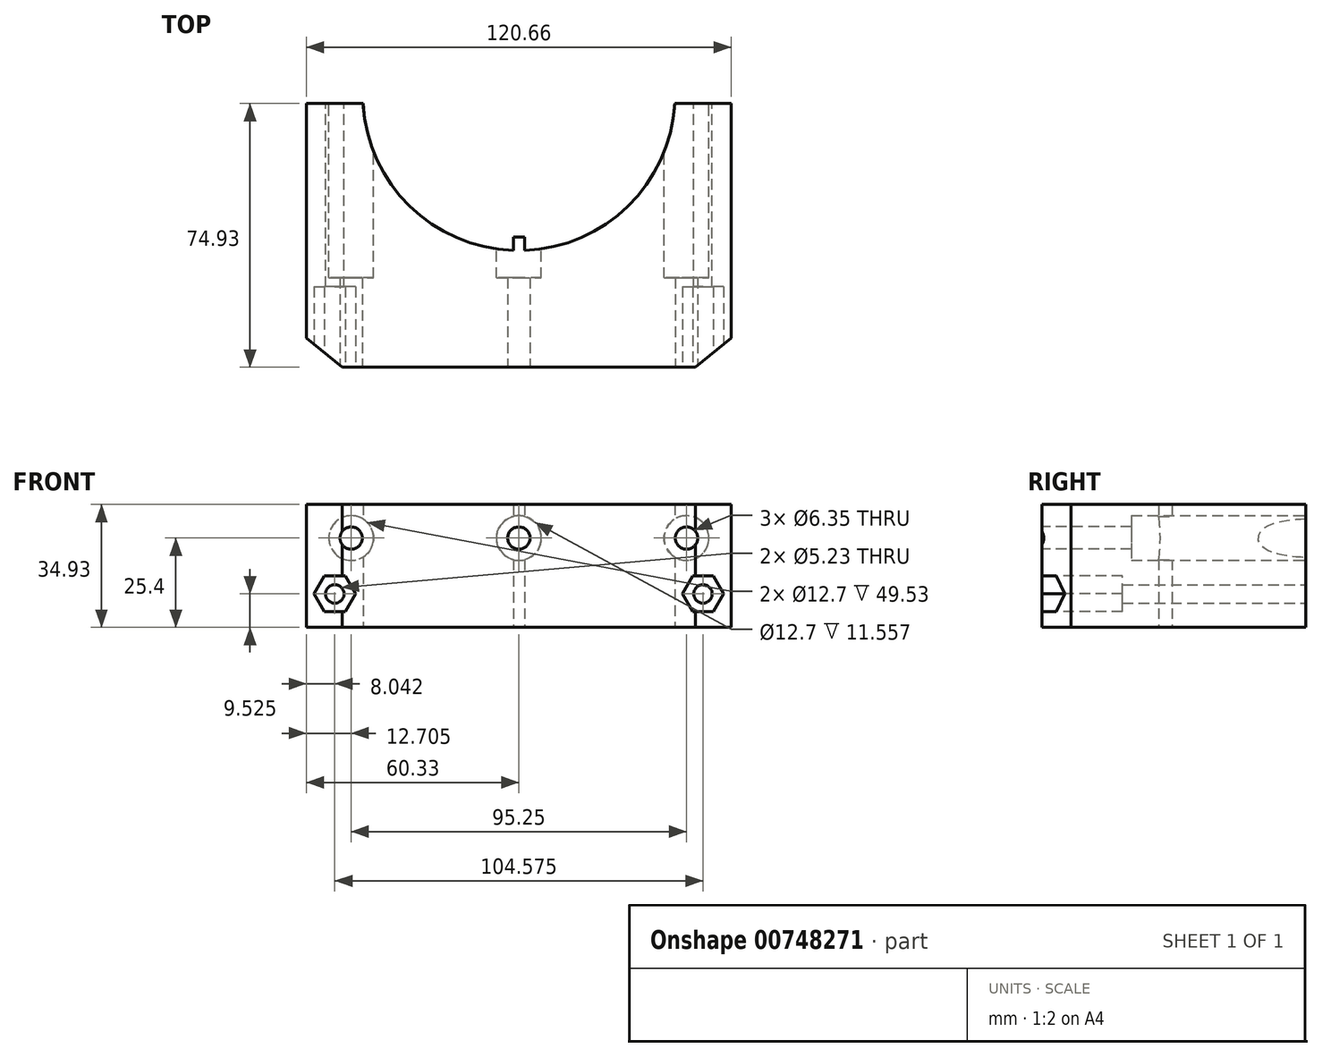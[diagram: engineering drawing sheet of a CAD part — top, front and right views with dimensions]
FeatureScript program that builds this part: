
annotation { "Feature Type Name" : "Feature", "Feature Type Description" : "" }
export const myFeature = defineFeature(function(context is Context, id is Id, definition is map)
    precondition{}
    {
        {
            var Q0;
            Q0=qCreatedBy(makeId("Top.planeOp"),FACE);
            var sketch = newSketch(context, id + "F0", { "sketchPlane" : qUnion([Q0])});
            skArc(sketch, "E0", {"start": v(-44.25, -2.54) * mm, "mid": v(-31, -31.68) * mm, "end": v(-1.59, -44.3) * mm});
            skLineSegment(sketch, "E1.bottom", {"start": v(60.32, -77.47) * mm, "end": v(-60.33, -77.47) * mm, "construction": true});
            skLineSegment(sketch, "E1.top", {"start": v(60.33, 77.47) * mm, "end": v(-60.32, 77.47) * mm, "construction": true});
            skLineSegment(sketch, "E1.left", {"start": v(60.33, -77.47) * mm, "end": v(60.33, 77.47) * mm, "construction": true});
            skLineSegment(sketch, "E1.right", {"start": v(-60.33, -77.47) * mm, "end": v(-60.32, 77.47) * mm, "construction": true});
            skLineSegment(sketch, "E2", {"start": v(-60.33, 0) * mm, "end": v(60.32, 0) * mm, "construction": true});
            skLineSegment(sketch, "E3.0", {"start": v(-60.33, -2.54) * mm, "end": v(60.32, -2.54) * mm, "construction": true});
            skLineSegment(sketch, "E4", {"start": v(-44.25, -2.54) * mm, "end": v(-60.33, -2.54) * mm});
            skLineSegment(sketch, "E5", {"start": v(-60.33, -2.54) * mm, "end": v(-60.33, -69.19) * mm});
            skLineSegment(sketch, "E6", {"start": v(-50.17, -77.47) * mm, "end": v(50.16, -77.47) * mm});
            skLineSegment(sketch, "E7", {"start": v(60.32, -69.19) * mm, "end": v(60.32, -2.54) * mm});
            skLineSegment(sketch, "E8", {"start": v(60.32, -2.54) * mm, "end": v(44.25, -2.54) * mm});
            skLineSegment(sketch, "E9.0", {"start": v(-50.17, -2.54) * mm, "end": v(-50.17, -77.47) * mm, "construction": true});
            skLineSegment(sketch, "E10.0", {"start": v(50.16, -77.47) * mm, "end": v(50.16, -2.54) * mm, "construction": true});
            skLineSegment(sketch, "E11.0", {"start": v(-60.33, -69.19) * mm, "end": v(60.32, -69.19) * mm, "construction": true});
            skLineSegment(sketch, "E12", {"start": v(-60.33, -69.19) * mm, "end": v(-50.17, -77.47) * mm});
            skLineSegment(sketch, "E13", {"start": v(60.32, -69.19) * mm, "end": v(50.16, -77.47) * mm});
            skLineSegment(sketch, "E14", {"start": v(0, -77.47) * mm, "end": v(0, 0) * mm, "construction": true});
            skLineSegment(sketch, "E15.0", {"start": v(1.59, -77.47) * mm, "end": v(1.59, 0) * mm});
            skLineSegment(sketch, "E16.0", {"start": v(-1.59, -77.47) * mm, "end": v(-1.59, 0) * mm});
            skPoint(sketch, "E17", {"position": v(0, -40.51) * mm});
            skLineSegment(sketch, "E18", {"start": v(0, -40.51) * mm, "end": v(-1.59, -40.51) * mm, "construction": true});
            skLineSegment(sketch, "E19", {"start": v(0, -40.51) * mm, "end": v(1.59, -40.51) * mm, "construction": true});
            skLineSegment(sketch, "E20", {"start": v(-1.59, -40.51) * mm, "end": v(1.59, -40.51) * mm});
            skArc(sketch, "E21.trimOffspring", {"start": v(1.59, -44.3) * mm, "mid": v(31, -31.68) * mm, "end": v(44.25, -2.54) * mm});
            skSolve(sketch);
        }
        {
            var Q0;
            Q0 = qSketchRegion(id + "F0", true);
            extrude(context, id + "F1", {"entities" : qUnion([Q0]), "depth" : 34.92 * mm, "offsetDistance" : 25.4 * mm});
        }
        {
            var Q0;
            Q0=makeQuery(id+"F1.opExtrude","SWEPT_FACE",FACE,{"disambiguationData":[OSD([sQuery(id+"F0.wireOp",EDGE,"E8")])]});
            var sketch = newSketch(context, id + "F2", { "sketchPlane" : qUnion([Q0])});
            skLineSegment(sketch, "E22", {"start": v(-52.29, 34.93) * mm, "end": v(-52.29, 0) * mm, "construction": true});
            skLineSegment(sketch, "E23", {"start": v(-60.32, 9.53) * mm, "end": v(-60.32, 9.53) * mm});
            skCircle(sketch, "E24", {"center": v(-52.29, 9.53) * mm, "radius": 2.62 * mm});
            skSolve(sketch);
        }
        {
            var Q0;
            Q0 = qSketchRegion(id + "F2", true);
            extrude(context, id + "F3", {"entities" : qUnion([Q0]), "operationType" : NewBodyOperationType.REMOVE, "endBound" : BoundingType.THROUGH_ALL, "oppositeDirection" : true, "depth" : 25.4 * mm, "offsetDistance" : 25.4 * mm});
        }
        {
            var Q0;
            Q0=makeQuery(id+"F1.opExtrude","SWEPT_FACE",FACE,{"disambiguationData":[OSD([sQuery(id+"F0.wireOp",EDGE,"E4")])]});
            var sketch = newSketch(context, id + "F4", { "sketchPlane" : qUnion([Q0])});
            skLineSegment(sketch, "E25", {"start": v(52.29, 34.93) * mm, "end": v(52.29, 0) * mm, "construction": true});
            skLineSegment(sketch, "E26", {"start": v(44.25, 9.53) * mm, "end": v(60.33, 9.53) * mm, "construction": true});
            skCircle(sketch, "E27", {"center": v(52.29, 9.53) * mm, "radius": 2.62 * mm});
            skSolve(sketch);
        }
        {
            var Q0;
            Q0 = qSketchRegion(id + "F4", true);
            extrude(context, id + "F5", {"entities" : qUnion([Q0]), "operationType" : NewBodyOperationType.REMOVE, "endBound" : BoundingType.THROUGH_ALL, "oppositeDirection" : true, "depth" : 25.4 * mm, "offsetDistance" : 25.4 * mm});
        }
        {
            var Q0;
            Q0=makeQuery(id+"F1.opExtrude","SWEPT_FACE",FACE,{"disambiguationData":[OSD([sQuery(id+"F0.wireOp",EDGE,"E6")])]});
            var sketch = newSketch(context, id + "F6", { "sketchPlane" : qUnion([Q0])});
            skLineSegment(sketch, "E28", {"start": v(-60.33, 25.4) * mm, "end": v(60.33, 25.4) * mm, "construction": true});
            skCircle(sketch, "E29", {"center": v(-47.63, 25.4) * mm, "radius": 3.18 * mm});
            skCircle(sketch, "E30", {"center": v(47.63, 25.4) * mm, "radius": 3.18 * mm});
            skCircle(sketch, "E31", {"center": v(0, 25.4) * mm, "radius": 3.18 * mm});
            skLineSegment(sketch, "E32", {"start": v(0, 0) * mm, "end": v(0, 34.93) * mm, "construction": true});
            skSolve(sketch);
        }
        {
            var Q0;
            Q0 = qSketchRegion(id + "F6", true);
            extrude(context, id + "F7", {"entities" : qUnion([Q0]), "operationType" : NewBodyOperationType.REMOVE, "endBound" : BoundingType.THROUGH_ALL, "oppositeDirection" : true, "depth" : 25.4 * mm, "offsetDistance" : 25.4 * mm});
        }
        {
            var Q0;
            Q0=makeQuery(id+"F1.opExtrude","SWEPT_FACE",FACE,{"disambiguationData":[OSD([sQuery(id+"F0.wireOp",EDGE,"E8")])]});
            var sketch = newSketch(context, id + "F8", { "sketchPlane" : qUnion([Q0])});
            skCircle(sketch, "E33", {"center": v(-47.63, 25.4) * mm, "radius": 6.35 * mm});
            skLineSegment(sketch, "E34", {"start": v(-47.63, 25.4) * mm, "end": v(47.63, 25.4) * mm, "construction": true});
            skCircle(sketch, "E35", {"center": v(0, 25.4) * mm, "radius": 6.35 * mm});
            skCircle(sketch, "E36", {"center": v(47.63, 25.4) * mm, "radius": 6.35 * mm});
            skSolve(sketch);
        }
        {
            var Q0;
            Q0 = qSketchRegion(id + "F8", true);
            extrude(context, id + "F9", {"entities" : qUnion([Q0]), "operationType" : NewBodyOperationType.REMOVE, "oppositeDirection" : true, "depth" : 49.53 * mm, "offsetDistance" : 25.4 * mm});
        }
        {
            var Q0;
            Q0=makeQuery(id+"F1.opExtrude","SWEPT_FACE",FACE,{"disambiguationData":[OSD([sQuery(id+"F0.wireOp",EDGE,"E6")])]});
            var sketch = newSketch(context, id + "F10", { "sketchPlane" : qUnion([Q0])});
            skCircle(sketch, "E37.cCircle", {"center": v(-52.29, 9.53) * mm, "radius": 5.08 * mm, "construction": true});
            skLineSegment(sketch, "E37.0", {"start": v(-46.42, 9.52) * mm, "end": v(-49.35, 4.45) * mm});
            skLineSegment(sketch, "E37.1", {"start": v(-49.35, 4.45) * mm, "end": v(-55.22, 4.45) * mm});
            skLineSegment(sketch, "E37.2", {"start": v(-55.22, 4.45) * mm, "end": v(-58.15, 9.53) * mm});
            skLineSegment(sketch, "E37.3", {"start": v(-58.15, 9.53) * mm, "end": v(-55.22, 14.6) * mm});
            skLineSegment(sketch, "E37.4", {"start": v(-55.22, 14.6) * mm, "end": v(-49.35, 14.6) * mm});
            skLineSegment(sketch, "E37.5", {"start": v(-49.35, 14.6) * mm, "end": v(-46.42, 9.52) * mm});
            skPoint(sketch, "E37.0.midPoint", {"position": v(-47.89, 6.98) * mm});
            skLineSegment(sketch, "E38", {"start": v(-52.29, 9.53) * mm, "end": v(52.29, 9.53) * mm, "construction": true});
            skCircle(sketch, "E39.cCircle", {"center": v(52.29, 9.53) * mm, "radius": 5.08 * mm, "construction": true});
            skLineSegment(sketch, "E39.0", {"start": v(46.42, 9.53) * mm, "end": v(49.35, 14.6) * mm});
            skLineSegment(sketch, "E39.1", {"start": v(49.35, 14.6) * mm, "end": v(55.22, 14.6) * mm});
            skLineSegment(sketch, "E39.2", {"start": v(55.22, 14.6) * mm, "end": v(58.15, 9.52) * mm});
            skLineSegment(sketch, "E39.3", {"start": v(58.15, 9.53) * mm, "end": v(55.22, 4.45) * mm});
            skLineSegment(sketch, "E39.4", {"start": v(55.22, 4.45) * mm, "end": v(49.35, 4.45) * mm});
            skLineSegment(sketch, "E39.5", {"start": v(49.35, 4.44) * mm, "end": v(46.42, 9.53) * mm});
            skPoint(sketch, "E39.0.midPoint", {"position": v(47.89, 12.07) * mm});
            skLineSegment(sketch, "E40.1", {"start": v(-46.42, 9.53) * mm, "end": v(-49.35, 4.45) * mm});
            skLineSegment(sketch, "E40.3", {"start": v(-55.22, 4.44) * mm, "end": v(-58.15, 9.53) * mm});
            skPoint(sketch, "E40.0.midPoint", {"position": v(-47.89, 12.07) * mm});
            skLineSegment(sketch, "E41.2", {"start": v(49.35, 4.45) * mm, "end": v(46.42, 9.53) * mm});
            skLineSegment(sketch, "E41.5", {"start": v(55.22, 14.6) * mm, "end": v(58.15, 9.53) * mm});
            skPoint(sketch, "E41.0.midPoint", {"position": v(56.69, 6.98) * mm});
            skSolve(sketch);
        }
        {
            var Q0;
            Q0 = qSketchRegion(id + "F10", true);
            extrude(context, id + "F11", {"entities" : qUnion([Q0]), "operationType" : NewBodyOperationType.REMOVE, "oppositeDirection" : true, "depth" : 22.86 * mm, "offsetDistance" : 25.4 * mm});
        }
        {
            var Q0;
            Q0=makeQuery(id+"F1.opExtrude","CAP_FACE",FACE,{"disambiguationData":[OSD([sQuery(id+"F0.wireOp",EDGE,"E4"),sQuery(id+"F0.wireOp",EDGE,"E5"),sQuery(id+"F0.wireOp",EDGE,"E6"),sQuery(id+"F0.wireOp",EDGE,"E7"),sQuery(id+"F0.wireOp",EDGE,"E8"),sQuery(id+"F0.wireOp",EDGE,"AukQrrzD-dbZz-uGUV-CgoS-Y1ikJe1PoGYa"),sQuery(id+"F0.wireOp",EDGE,"e4Z8ujvW-3aFd-mzqK-Fj9L-4rO8kLBsugpI"),sQuery(id+"F0.wireOp",EDGE,"Cb9sT8sm-J7Pc-vMKr-wsvC-wKcfh4iLigrn"),sQuery(id+"F0.wireOp",EDGE,"yfd3Dl8R-1cPx-KhIc-XqcL-W2j3U9ra6mNd"),sQuery(id+"F0.wireOp",EDGE,"E6SXMi67-y4CI-j7KQ-ZSRJ-Tu2jy88v5S8K"),sQuery(id+"F0.wireOp",EDGE,"E12"),sQuery(id+"F0.wireOp",EDGE,"E13")])],"isStart":false});
            var sketch = newSketch(context, id + "F12", { "sketchPlane" : qUnion([Q0])});
            skLineSegment(sketch, "E42", {"start": v(0, -77.47) * mm, "end": v(0, -44.32) * mm, "construction": true});
            skLineSegment(sketch, "E43", {"start": v(0, -44.32) * mm, "end": v(0, -41.78) * mm, "construction": true});
            skLineSegment(sketch, "E44.0", {"start": v(1.59, -44.32) * mm, "end": v(1.59, -41.78) * mm, "construction": true});
            skLineSegment(sketch, "E45.0", {"start": v(-1.59, -44.32) * mm, "end": v(-1.59, -41.78) * mm, "construction": true});
            skPoint(sketch, "E46", {"position": v(1.59, -44.3) * mm});
            skPoint(sketch, "E47", {"position": v(-1.59, -44.32) * mm});
            skLineSegment(sketch, "E48", {"start": v(-1.59, -44.32) * mm, "end": v(-1.59, -41.78) * mm});
            skLineSegment(sketch, "E49", {"start": v(-1.59, -41.78) * mm, "end": v(1.59, -41.78) * mm});
            skLineSegment(sketch, "E50", {"start": v(1.59, -41.78) * mm, "end": v(1.59, -44.3) * mm});
            skLineSegment(sketch, "E51", {"start": v(-1.59, -44.32) * mm, "end": v(1.59, -44.3) * mm});
            skSolve(sketch);
        }
        {
            var Q0;
            Q0 = qSketchRegion(id + "F12", true);
            extrude(context, id + "F13", {"entities" : qUnion([Q0]), "operationType" : NewBodyOperationType.ADD, "oppositeDirection" : true, "depth" : 2.54 * mm, "offsetDistance" : 25.4 * mm});
        }
    });
